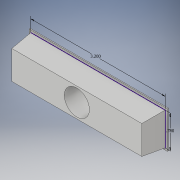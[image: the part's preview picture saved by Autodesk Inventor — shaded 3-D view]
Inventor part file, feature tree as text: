
AUTODESK INVENTOR PART (.ipt)
format: ipt  version: 2019 (Build 230136000, 136)  size: 140,288 bytes
history: native  units: in
note: dims shown in document units (in); Inventor stores cm internally (conversion verified against a paired STEP export)
features: extrude x3, sketch x3, other x2, plane x1, loft x1, hole x1, projected_geometry x1
ambient origin geometry x8: Origin, YZ Plane, XZ Plane, XY Plane, X Axis, Y Axis, Z Axis, Center Point
bodies: Solid1 (feature_tree)
feature tree (12):
  extrude  "Extrusion1"  Depth=0.78in
  plane  "Work Plane1"
  extrude  "Extrusion2"  Depth=0.005in
  loft  "Loft1"
  sketch  "Sketch3"  dims[d5=0.05in d6=0.005in d7=0.0in d8=0.0in d9=90.0deg d10=0.0in d11=90.0deg d12=0.05in d13=0.025in d14=0.0in d15=0.6in d16=0.6in d17=0.75in d18=0.375in d19=0.25in d20=0.5635in d21=0.432in d22=0.8108in]
  extrude  "Extrusion3"  TaperAngle=0.0deg  [1 undecoded]
  hole  "Hole1"  [1 undecoded]
  sketch  "Sketch1"  dims[d0=3.2in d1=0.78in]
  sketch  "Sketch2"  dims[d2=0.005in d3=0.0in d4=0.5in]
  projected_geometry  "Projected Loop1"
  other  "Edges1"
  other  "Edges2"
note: 2 required parameter values undecoded (feature->parameter linkage not recoverable at this tier; creation-order binding heuristic only, values carry confidence <= 0.55)
